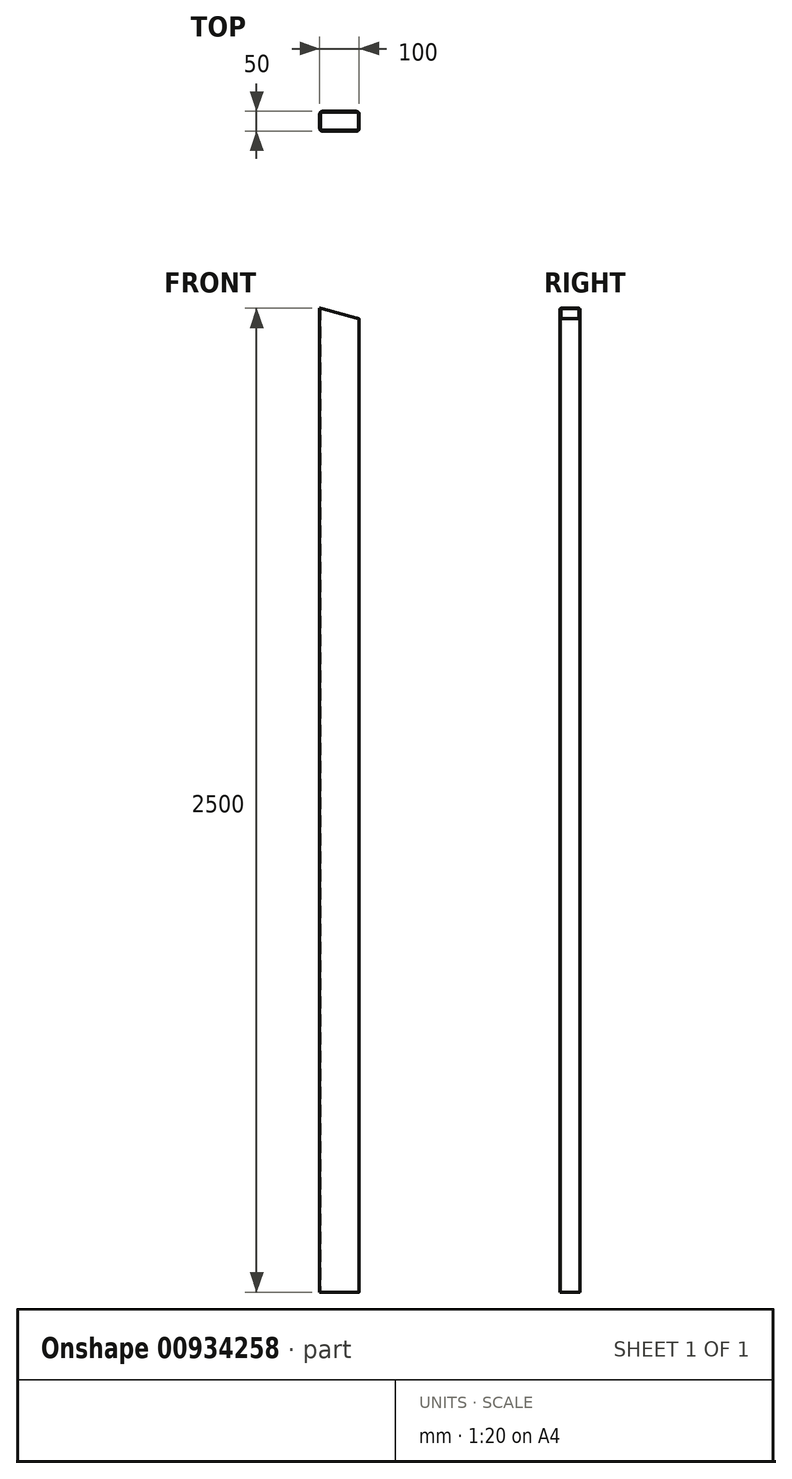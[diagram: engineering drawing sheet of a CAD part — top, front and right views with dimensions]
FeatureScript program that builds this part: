
annotation { "Feature Type Name" : "Feature", "Feature Type Description" : "" }
export const myFeature = defineFeature(function(context is Context, id is Id, definition is map)
    precondition{}
    {
        {
            var Q0;
            Q0=qCreatedBy(makeId("Top.planeOp"),FACE);
            var sketch = newSketch(context, id + "F0", { "sketchPlane" : qUnion([Q0])});
            skLineSegment(sketch, "E0.bottom", {"start": v(-44, 25) * mm, "end": v(44, 25) * mm});
            skLineSegment(sketch, "E0.top", {"start": v(-44, -25) * mm, "end": v(44, -25) * mm});
            skLineSegment(sketch, "E0.left", {"start": v(-50, 19) * mm, "end": v(-50, -19) * mm});
            skLineSegment(sketch, "E0.right", {"start": v(50, 19) * mm, "end": v(50, -19) * mm});
            skPoint(sketch, "E1.visualSharp", {"position": v(-50, 25) * mm});
            skArc(sketch, "E1.filletArc", {"start": v(-44, 25) * mm, "mid": v(-48.24, 23.24) * mm, "end": v(-50, 19) * mm});
            skPoint(sketch, "E2.visualSharp", {"position": v(-50, -25) * mm});
            skArc(sketch, "E2.filletArc", {"start": v(-50, -19) * mm, "mid": v(-48.24, -23.24) * mm, "end": v(-44, -25) * mm});
            skPoint(sketch, "E3.visualSharp", {"position": v(50, -25) * mm});
            skArc(sketch, "E3.filletArc", {"start": v(44, -25) * mm, "mid": v(48.24, -23.24) * mm, "end": v(50, -19) * mm});
            skPoint(sketch, "E4.visualSharp", {"position": v(50, 25) * mm});
            skArc(sketch, "E4.filletArc", {"start": v(50, 19) * mm, "mid": v(48.24, 23.24) * mm, "end": v(44, 25) * mm});
            skArc(sketch, "E5.0", {"start": v(-44, 23) * mm, "mid": v(-46.83, 21.83) * mm, "end": v(-48, 19) * mm});
            skLineSegment(sketch, "E5.1", {"start": v(-48, 19) * mm, "end": v(-48, -19) * mm});
            skLineSegment(sketch, "E5.2", {"start": v(-44, 23) * mm, "end": v(44, 23) * mm});
            skArc(sketch, "E5.3", {"start": v(-48, -19) * mm, "mid": v(-46.83, -21.83) * mm, "end": v(-44, -23) * mm});
            skArc(sketch, "E5.4", {"start": v(48, 19) * mm, "mid": v(46.83, 21.83) * mm, "end": v(44, 23) * mm});
            skLineSegment(sketch, "E5.5", {"start": v(48, 19) * mm, "end": v(48, -19) * mm});
            skArc(sketch, "E5.6", {"start": v(44, -23) * mm, "mid": v(46.83, -21.83) * mm, "end": v(48, -19) * mm});
            skLineSegment(sketch, "E5.7", {"start": v(-44, -23) * mm, "end": v(44, -23) * mm});
            skSolve(sketch);
        }
        {
            var Q0;
            Q0=makeQuery(id+"F0.imprint","IMPRINT",FACE,{"disambiguationData":[TD([[makeQuery(id+"F0.imprint","IMPRINT",EDGE,{"derivedFrom":sQuery(id+"F0.wireOp",EDGE,"E0.bottom")}),-1.0]])]});
            extrude(context, id + "F1", {"entities" : qUnion([Q0]), "endBound" : BoundingType.SYMMETRIC, "depth" : 2500 * mm, "offsetDistance" : 25 * mm});
        }
        {
            var Q0;
            Q0=makeQuery(id+"F1.opExtrude","SWEPT_FACE",FACE,{"disambiguationData":[OSD([sQuery(id+"F0.wireOp",EDGE,"E0.top")])]});
            var sketch = newSketch(context, id + "F2", { "sketchPlane" : qUnion([Q0])});
            skPoint(sketch, "E6.0", {"position": v(-50, 1250) * mm});
            skLineSegment(sketch, "E7.0", {"start": v(-50, 1250) * mm, "end": v(-50, -1250) * mm});
            skLineSegment(sketch, "E8.0", {"start": v(50, 1250) * mm, "end": v(50, -1250) * mm});
            skLineSegment(sketch, "E9", {"start": v(-50, 1250) * mm, "end": v(50, 1223.2) * mm});
            skLineSegment(sketch, "E10", {"start": v(50, 1223.2) * mm, "end": v(50, 1250) * mm});
            skLineSegment(sketch, "E11", {"start": v(50, 1250) * mm, "end": v(-50, 1250) * mm});
            skSolve(sketch);
        }
        {
            var Q0;
            {var subQ0=sQuery(id+"F2.wireOp",EDGE,"E9");var subQ1=sQuery(id+"F2.wireOp",EDGE,"E8.0");var subQ2=makeQuery(id+"F2.imprint","INTERSECT",VERTEX,{"derivedFrom":[subQ1,subQ0]});Q0=makeQuery(id+"F2.imprint","IMPRINT",FACE,{"disambiguationData":[TD([[makeQuery(id+"F2.imprint","IMPRINT",EDGE,{"disambiguationData":[TD([[subQ2,1.0]])],"derivedFrom":subQ1}),-1.0]])]});}
            var Q1;
            {var subQ0=sQuery(id+"F2.wireOp",EDGE,"E9");var subQ1=sQuery(id+"F0.wireOp",EDGE,"E0.top");var subQ2=makeQuery(id+"F1.opExtrude","SWEPT_EDGE",EDGE,{"disambiguationData":[OSD([subQ1,sQuery(id+"F0.wireOp",EDGE,"E2.filletArc")])]});var subQ3=makeQuery(id+"F2.imprint","INTERSECT",VERTEX,{"derivedFrom":[subQ2,subQ0]});Q1=makeQuery(id+"F2.imprint","IMPRINT",FACE,{"disambiguationData":[TD([[makeQuery(id+"F2.imprint","IMPRINT",EDGE,{"disambiguationData":[TD([[subQ3,-1.0]])],"derivedFrom":subQ0}),1.0]])]});}
            var Q2;
            {var subQ0=sQuery(id+"F2.wireOp",EDGE,"E11");var subQ1=sQuery(id+"F2.wireOp",EDGE,"E9");var subQ2=makeQuery(id+"F2.imprint","INTERSECT",VERTEX,{"derivedFrom":[subQ1,subQ0]});Q2=makeQuery(id+"F2.imprint","IMPRINT",FACE,{"disambiguationData":[TD([[makeQuery(id+"F2.imprint","IMPRINT",EDGE,{"disambiguationData":[TD([[subQ2,-1.0]])],"derivedFrom":subQ1}),1.0]])]});}
            extrude(context, id + "F3", {"entities" : qUnion([Q0, Q1, Q2]), "operationType" : NewBodyOperationType.REMOVE, "endBound" : BoundingType.THROUGH_ALL, "oppositeDirection" : true, "depth" : 25 * mm, "offsetDistance" : 25 * mm});
        }
    });
